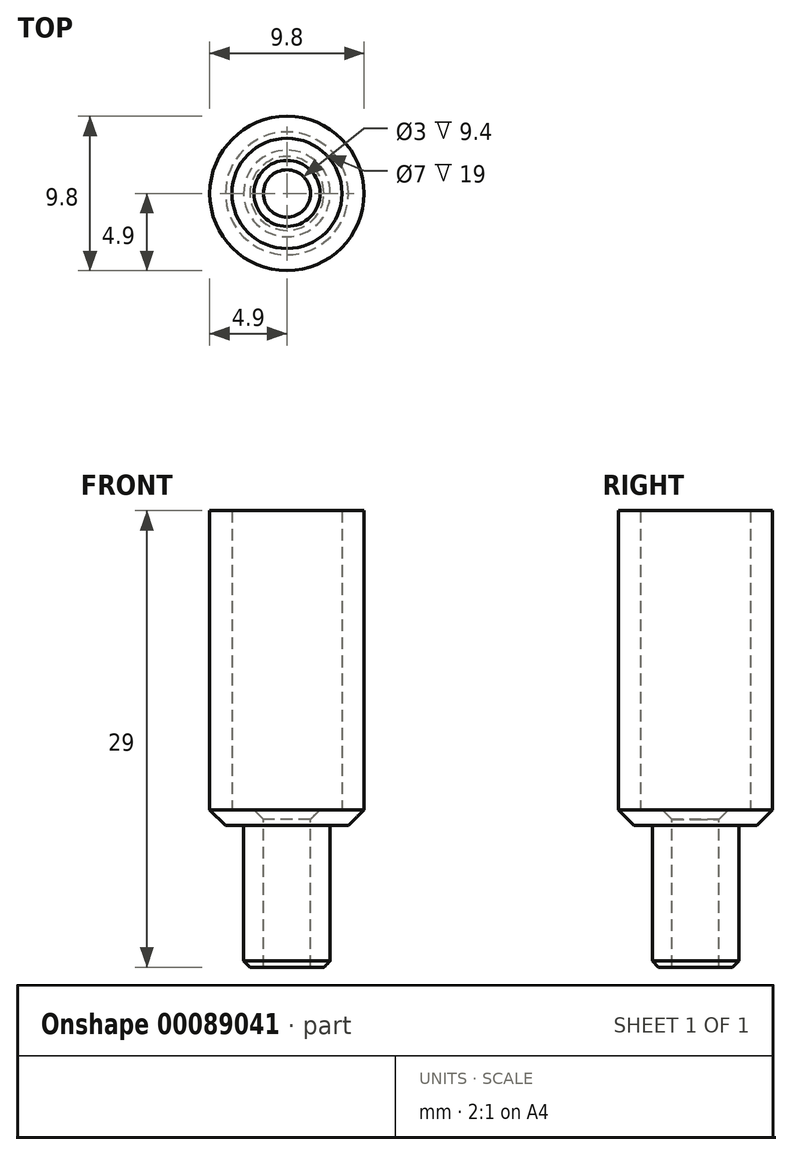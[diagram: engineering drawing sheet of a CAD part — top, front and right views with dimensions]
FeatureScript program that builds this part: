
annotation { "Feature Type Name" : "Feature", "Feature Type Description" : "" }
export const myFeature = defineFeature(function(context is Context, id is Id, definition is map)
    precondition{}
    {
        {
            var Q0;
            Q0=qCreatedBy(makeId("Top.planeOp"),FACE);
            var sketch = newSketch(context, id + "F0", { "sketchPlane" : qUnion([Q0])});
            skCircle(sketch, "E0", {"center": v(0, 0) * mm, "radius": 1.5 * mm});
            skCircle(sketch, "E1", {"center": v(0, 0) * mm, "radius": 2.75 * mm});
            skCircle(sketch, "E2", {"center": v(0, 0) * mm, "radius": 3.5 * mm});
            skCircle(sketch, "E3", {"center": v(0, 0) * mm, "radius": 4.9 * mm});
            skSolve(sketch);
        }
        {
            var Q0;
            Q0=makeQuery(id+"F0.imprint","IMPRINT",FACE,{"disambiguationData":[TD([[makeQuery(id+"F0.imprint","IMPRINT",EDGE,{"derivedFrom":sQuery(id+"F0.wireOp",EDGE,"E0")}),-1.0]])]});
            extrude(context, id + "F1", {"entities" : qUnion([Q0]), "oppositeDirection" : true, "depth" : 9 * mm});
        }
        {
            var Q0;
            Q0=makeQuery(id+"F0.imprint","IMPRINT",FACE,{"disambiguationData":[TD([[makeQuery(id+"F0.imprint","IMPRINT",EDGE,{"derivedFrom":sQuery(id+"F0.wireOp",EDGE,"E1")}),-1.0]])]});
            var Q1;
            Q1=makeQuery(id+"F0.imprint","IMPRINT",FACE,{"disambiguationData":[TD([[makeQuery(id+"F0.imprint","IMPRINT",EDGE,{"derivedFrom":sQuery(id+"F0.wireOp",EDGE,"E0")}),-1.0]])]});
            extrude(context, id + "F2", {"entities" : qUnion([Q0, Q1]), "operationType" : NewBodyOperationType.ADD, "depth" : 1 * mm});
        }
        {
            var Q0;
            Q0=makeQuery(id+"F0.imprint","IMPRINT",FACE,{"disambiguationData":[TD([[makeQuery(id+"F0.imprint","IMPRINT",EDGE,{"derivedFrom":sQuery(id+"F0.wireOp",EDGE,"E2")}),-1.0]])]});
            extrude(context, id + "F3", {"entities" : qUnion([Q0]), "operationType" : NewBodyOperationType.ADD, "depth" : 20 * mm});
        }
        {
            var Q0;
            Q0=makeQuery(id+"F3.opExtrude","CAP_EDGE",EDGE,{"disambiguationData":[OSD([sQuery(id+"F0.wireOp",EDGE,"E3")])],"isStart":true});
            chamfer(context, id + "F4", {"entities" : qUnion([Q0]), "width" : 1 * mm, "tangentPropagation" : true});
        }
        {
            var Q0;
            Q0=makeQuery(id+"F2.opExtrude","CAP_EDGE",EDGE,{"disambiguationData":[OSD([sQuery(id+"F0.wireOp",EDGE,"E0")])],"isStart":false});
            chamfer(context, id + "F5", {"entities" : qUnion([Q0]), "width" : .6 * mm, "tangentPropagation" : true});
        }
        {
            var Q0;
            Q0=makeQuery(id+"F1.opExtrude","CAP_EDGE",EDGE,{"disambiguationData":[OSD([sQuery(id+"F0.wireOp",EDGE,"E1")])],"isStart":false});
            chamfer(context, id + "F6", {"entities" : qUnion([Q0]), "width" : .4 * mm, "tangentPropagation" : true});
        }
    });
